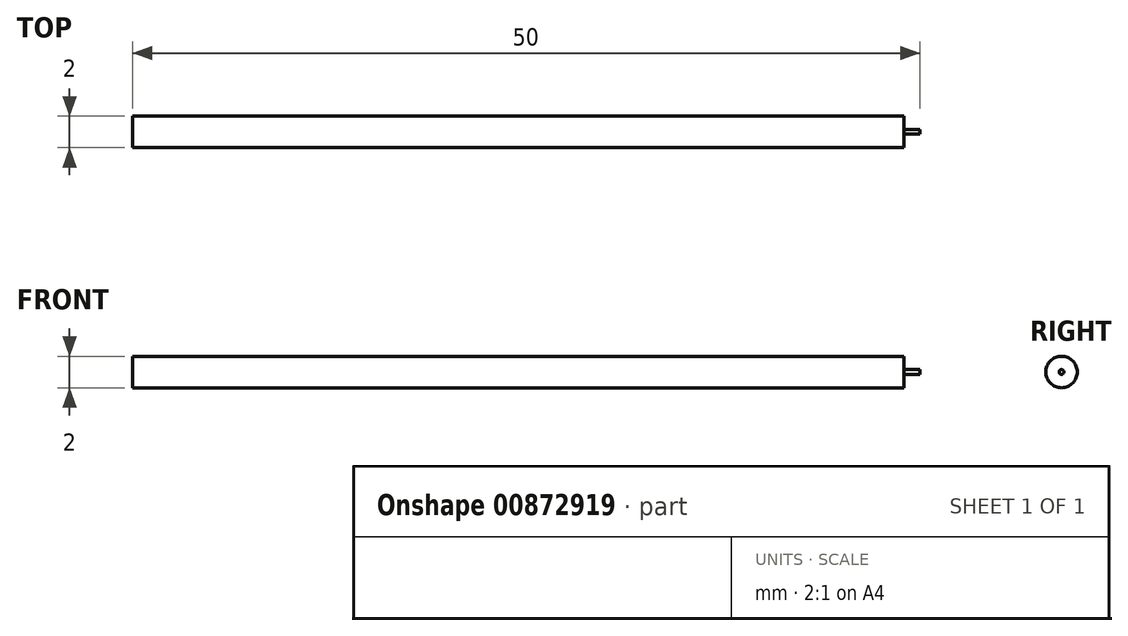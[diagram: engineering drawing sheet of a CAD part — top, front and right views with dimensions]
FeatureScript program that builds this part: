
annotation { "Feature Type Name" : "Feature", "Feature Type Description" : "" }
export const myFeature = defineFeature(function(context is Context, id is Id, definition is map)
    precondition{}
    {
        {
            var Q0;
            Q0=qCreatedBy(makeId("Front.planeOp"),FACE);
            var sketch = newSketch(context, id + "F0", { "sketchPlane" : qUnion([Q0])});
            skLineSegment(sketch, "E0.bottom", {"start": v(24.5, 0) * mm, "end": v(-24.5, 0) * mm});
            skLineSegment(sketch, "E0.top", {"start": v(24.5, -1) * mm, "end": v(-24.5, -1) * mm});
            skLineSegment(sketch, "E0.left", {"start": v(24.5, 0) * mm, "end": v(24.5, -1) * mm});
            skLineSegment(sketch, "E0.right", {"start": v(-24.5, 0) * mm, "end": v(-24.5, -1) * mm});
            skLineSegment(sketch, "E1.bottom", {"start": v(25.5, -0.15) * mm, "end": v(24.5, -0.15) * mm});
            skLineSegment(sketch, "E1.top", {"start": v(25.5, 0) * mm, "end": v(24.5, 0) * mm});
            skLineSegment(sketch, "E1.left", {"start": v(25.5, -0.15) * mm, "end": v(25.5, 0) * mm});
            skLineSegment(sketch, "E1.right", {"start": v(24.5, -0.15) * mm, "end": v(24.5, 0) * mm});
            skLineSegment(sketch, "E2", {"start": v(-29.03, 0) * mm, "end": v(37.21, 0) * mm, "construction": true});
            skSolve(sketch);
        }
        {
            var Q0;
            Q0 = qSketchRegion(id + "F0", true);
            var Q1;
            Q1=sQuery(id+"F0.wireOp",EDGE,"E2");
            revolve(context, id + "F1", {"surfaceOperationType" : NewSurfaceOperationType.NEW, "entities" : qUnion([Q0]), "axis" : qUnion([Q1]), "revolveType" : RevolveType.FULL, "oppositeDirection" : true});
        }
    });
